# Revit family: JAD_Neon_A5589_BIM_DE
name_source: partatom
category: Plumbing Fixtures
revit_build: Autodesk Revit MEP 2016 (Build: 20161004_0715(x64)
units: mm (PartAtom-declared; Revit-internal decimal feet)

## family parameters
Always vertical = No
Cut with Voids When Loaded = No
OmniClass Number = 23.45.55.17
OmniClass Title = Mixing Faucets
Part Type = Normal
Room Calculation Point = No
Round Connector Dimension = Use Diameter
Shared = No
Work Plane-Based = No

## types (1)
- A5589AA NEON kitchen mixer one hole high spout single lever hand
    Accessories = www.idealstandard.de\ersatzteile
    AssetType = Fixed
    BIMObjectName = ISI_IdealStandard_KitchenTaps_Neon_A5589AA
    BOSUseNativeGeometries = 1
    Brand = Ideal Standard
    Brand url = http://www.idealstandard.de
    CodePerformance = EN 817, DIN 4109, Gruppe 1
    Color = Chrome
    ConnectionType = Plumbing
    Cost = 0 $
    CurrencyUnit = €
    CurrentRevision = 1
    Date of publishing = 20/12/2017
    Description = IS JADO Küchenarmatur mit hohem Auslauf Ausladung 200mm,Schwenkb. 360 Grad Chrom
    DurationUnit = Year
    Edition number = 1
    ExpectedLife = 25
    Features = IS JADO Küchenarmatur mit hohem Auslauf Ausladung 200mm,Schwenkb. 360 Grad Chrom
    Finish = Chrome
    IFC Classification = Sanitary Terminal
    IfcExportAs = IfcSanitaryTerminalType
    InletConnectionSize = 0 mm  [stored 0 ft]
    Installation instructions = http://www.idealstandard.de
    InstallationInstructions = www.idealstandard.de\produkte
    MainColor = Chrome
    MaintenanceInformation = www.idealstandard.de\produkte
    Manufacturer name = Ideal Standard
    ManufacturerURL = http://www.idealstandard.de
    Material = Brass
    Model = A5589AA
    ModelNumber = A5589AA
    ModelReference = IS JADO Küchenarmatur mit hohem Auslauf Ausladung 200mm,Schwenkb. 360 Grad Chrom
    Name = KitchenTaps_Neon_A5589AA
    NettWeight = 0 Kg
    Nominal height = 0
    Nominal width = 0
    NominalDepth = 234 mm  [stored 0.767717 ft]
    NominalHeight = 278 mm
    NominalLength = 234 mm  [stored 0.767717 ft]
    NominalWidth = 93 mm
    Product Guid = e5dbffd7-c675-40f7-85f9-848ea6d0b87f
    Product SKU = A5589AA
    Product data url = https://bimobject.com
    Product family = Sanitary
    Product name = IS JADO K??chenarmatur mit hohem Auslauf Ausladung 200mm,Schwenkb. 360 Grad Chrom
    Product url = http://www.idealstandard.de
    ProductInformation = www.idealstandard.de/produkte
    QR code = http://bimobject.com
    Shape = Sculptured
    Size = 93x234x278 mm
    Space = Internal
    SpareParts = www.idealstandard.de/ersatzteile
    Technical description = http://www.idealstandard.de
    URL = http://www.idealstandard.de
    Uniclass2015Title = Kitchen taps
    Uniclass2015Version = Products v1.1
    Version = 1
    VolumeUnits = Litres
    Weight Net (Kg) = 0

note: [stored X ft] marks values corroborated as IEEE doubles in the binary element streams (Revit-internal decimal feet)

## geometry (parser evidence)
native form markers: Blend x4, Sweep x1
no freeform markers — native parametric forms only
